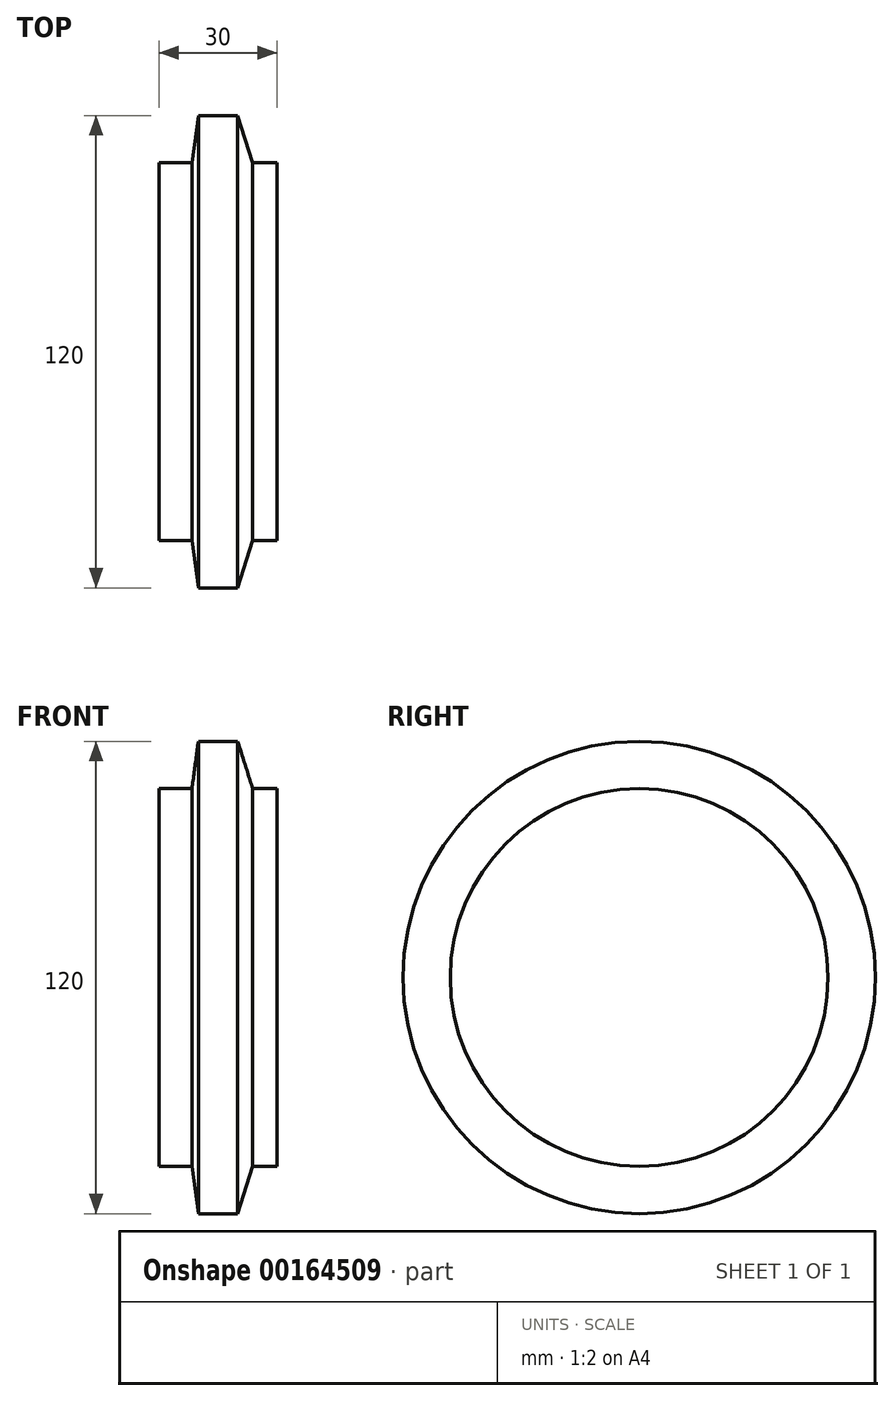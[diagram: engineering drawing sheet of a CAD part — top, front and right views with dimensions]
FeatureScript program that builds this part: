
annotation { "Feature Type Name" : "Feature", "Feature Type Description" : "" }
export const myFeature = defineFeature(function(context is Context, id is Id, definition is map)
    precondition{}
    {
        {
            var Q0;
            Q0=qCreatedBy(makeId("Front.planeOp"),FACE);
            var sketch = newSketch(context, id + "F3", { "sketchPlane" : qUnion([Q0])});
            skLineSegment(sketch, "E0", {"start": v(0, 0) * mm, "end": v(-10, 0) * mm});
            skLineSegment(sketch, "E1", {"start": v(-20, 12) * mm, "end": v(-20, 60) * mm});
            skLineSegment(sketch, "E2", {"start": v(-20, 60) * mm, "end": v(10, 60) * mm});
            skLineSegment(sketch, "E3", {"start": v(10, 60) * mm, "end": v(10, 12) * mm});
            skLineSegment(sketch, "E4", {"start": v(-10, 0) * mm, "end": v(0, 0) * mm});
            skLineSegment(sketch, "E5", {"start": v(-20, 12) * mm, "end": v(-11.64, 12) * mm});
            skLineSegment(sketch, "E6", {"start": v(-11.64, 12) * mm, "end": v(-10, 0) * mm});
            skLineSegment(sketch, "E7", {"start": v(3.8, 12) * mm, "end": v(10, 12) * mm});
            skLineSegment(sketch, "E8", {"start": v(3.8, 12) * mm, "end": v(0, 0) * mm});
            skPoint(sketch, "E9.orphan", {"position": v(10, 0) * mm});
            skPoint(sketch, "E10.orphan", {"position": v(-20, 0) * mm});
            skSolve(sketch);
        }
        {
            var Q0;
            Q0 = qSketchRegion(id + "F3", true);
            var Q1;
            Q1=sQuery(id+"F3.wireOp",EDGE,"E2");
            revolve(context, id + "F0", {"entities" : qUnion([Q0]), "axis" : qUnion([Q1]), "revolveType" : RevolveType.FULL});
        }
    });
